# Revit family: Data_Device-Network-Leviton-Splice_Tray-T5PLS
name_source: partatom
category: Data Devices
units: mm (PartAtom-declared; Revit-internal decimal feet)

## family parameters
Cut with Voids When Loaded = No
Host = Face
Maintain Annotation Orientation = Yes
OmniClass Number = 23.85.50.17
OmniClass Title = Communication and Data Processing Equipment
Part Type = Normal
Room Calculation Point = No
Round Connector Dimension = Use Diameter
Shared = Yes

## types (2) — shared parameters
Assembly Code = D5030600
Date Last Modified = September 28, 2023
Default Elevation = 24 "
Equipment Abbreviation = FST
Family Version = 1.0.0
Has ID Windows = No
Manufacturer = Leviton
Model Disclaimer = http://www.leviton.com
Product Documentation Link = https://www.leviton.com
Shielded = No
URL = http://www.leviton.com
zero-valued in all types: Minimum Order Quantity, Quantity per Package

## per-type parameters (varying)
| type | Adapter Material | Description | Part Description | z Is 12 Fibers | z Is 24 Fibers | z Leviton Type |
| 12-Fiber Splice Tray | Plastic - Leviton - Aqua | OPT-X SDX Engage Low Loss MTP Fiber Cassettes - OM3, 12-fiber, MPT to LC shuttered, C Polarity. | OPT-X SDX Engage Low Loss MTP Fiber Cassettes - OM3, 12-fiber, MPT to LC shuttered, C Polarity. | Yes | No | 1 |
| 24-Fiber Splice Tray | Plastic - Leviton - Blue | OPT-X SDX Engage Low Loss MTP Fiber Cassettes - OS2, 24-fiber, 2x12F MTP to LC shuttered, C Polarity. | OPT-X SDX Engage Low Loss MTP Fiber Cassettes - OS2, 24-fiber, 2x12F MTP to LC shuttered, C Polarity. | No | Yes | 2 |

## geometry (parser evidence)
native form markers: Blend x81, Sweep x9
no freeform markers — native parametric forms only
